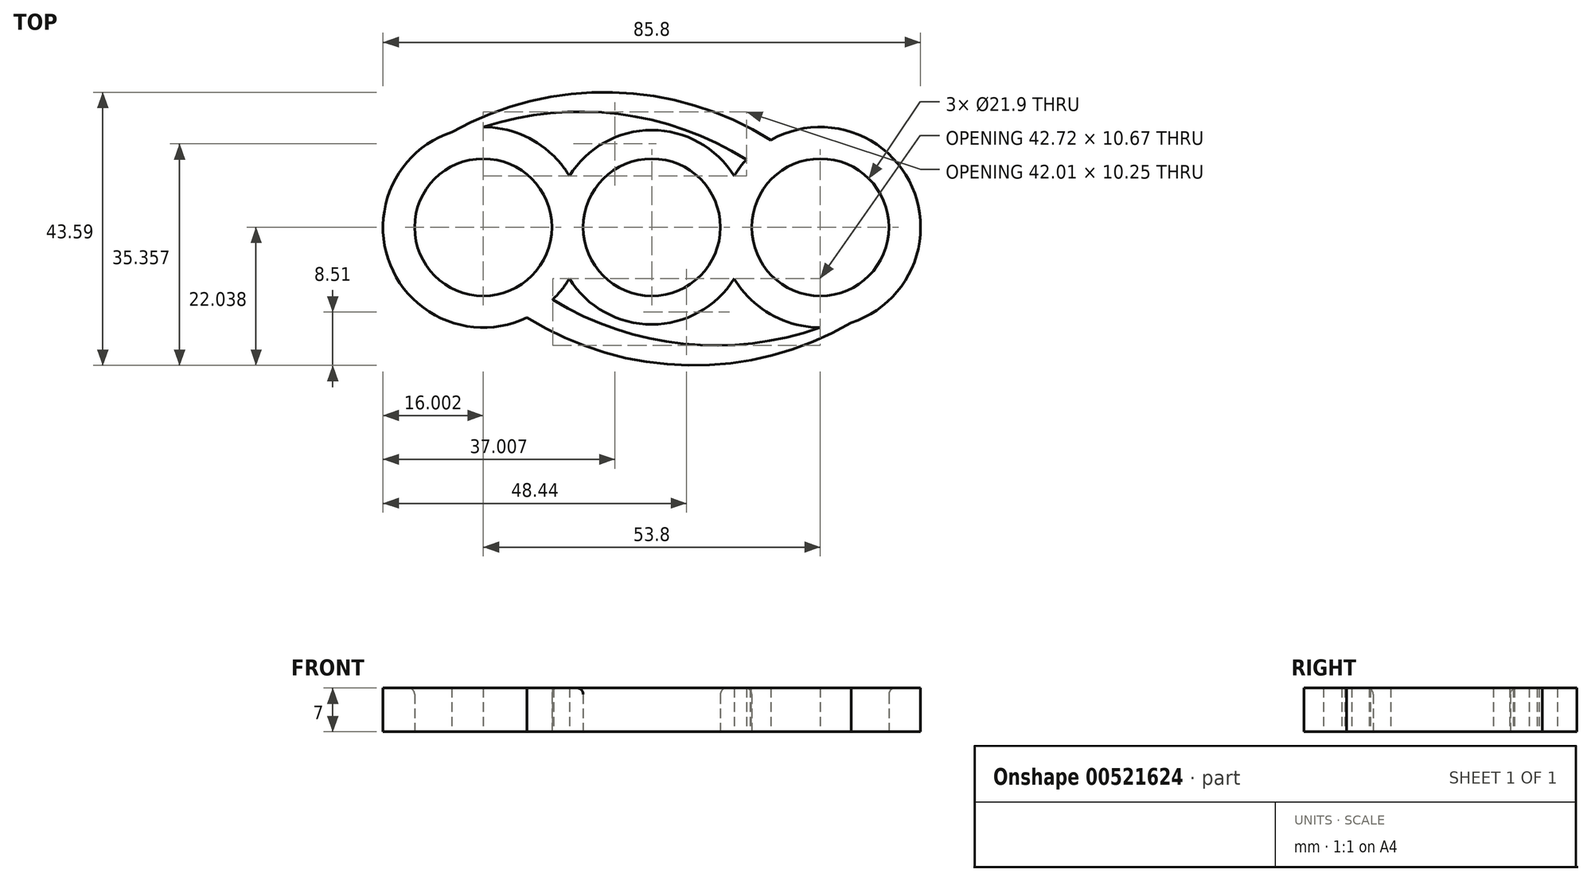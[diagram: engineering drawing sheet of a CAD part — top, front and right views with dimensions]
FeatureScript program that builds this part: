
annotation { "Feature Type Name" : "Feature", "Feature Type Description" : "" }
export const myFeature = defineFeature(function(context is Context, id is Id, definition is map)
    precondition{}
    {
        {
            var Q0;
            Q0=qCreatedBy(makeId("Top.planeOp"),FACE);
            var sketch = newSketch(context, id + "F0", { "sketchPlane" : qUnion([Q0])});
            skCircle(sketch, "E0", {"center": v(-8.38, 3.3) * mm, "radius": 10.95 * mm});
            skCircle(sketch, "E1", {"center": v(-35.28, 3.3) * mm, "radius": 10.95 * mm});
            skCircle(sketch, "E2", {"center": v(18.52, 3.3) * mm, "radius": 10.95 * mm});
            skCircle(sketch, "E3", {"center": v(-35.28, 3.3) * mm, "radius": 16 * mm});
            skCircle(sketch, "E4", {"center": v(-8.38, 3.3) * mm, "radius": 15.5 * mm});
            skCircle(sketch, "E5", {"center": v(18.52, 3.3) * mm, "radius": 16 * mm});
            skArc(sketch, "E6", {"start": v(-19.43, -7.57) * mm, "mid": v(-21.93, -7.1) * mm, "end": v(-24.2, -8.25) * mm});
            skPoint(sketch, "E6.startSnap0", {"position": v(-19.43, -4.4) * mm});
            skArc(sketch, "E7", {"start": v(7.47, -8.27) * mm, "mid": v(5.2, -7.11) * mm, "end": v(2.67, -7.57) * mm});
            skArc(sketch, "E8", {"start": v(2.67, 14.17) * mm, "mid": v(4.7, 13.59) * mm, "end": v(6.73, 14.12) * mm});
            skArc(sketch, "E9", {"start": v(-24.23, 14.87) * mm, "mid": v(-21.95, 13.7) * mm, "end": v(-19.43, 14.17) * mm});
            skArc(sketch, "E10", {"start": v(6.73, 14.12) * mm, "mid": v(-13.7, 21.37) * mm, "end": v(-35.28, 19.3) * mm});
            skArc(sketch, "E11", {"start": v(-24.2, -8.25) * mm, "mid": v(-3.34, -15.3) * mm, "end": v(18.52, -12.7) * mm});
            skArc(sketch, "E12", {"start": v(-28.3, -11.1) * mm, "mid": v(-2.54, -18.73) * mm, "end": v(23.46, -11.92) * mm});
            skArc(sketch, "E13", {"start": v(10.65, 17.23) * mm, "mid": v(-14.64, 24.83) * mm, "end": v(-40.28, 18.5) * mm});
            skSolve(sketch);
        }
        {
            var Q0;
            Q0=makeQuery(id+"F0.imprint","IMPRINT",FACE,{"disambiguationData":[TD([[makeQuery(id+"F0.imprint","IMPRINT",EDGE,{"derivedFrom":sQuery(id+"F0.wireOp",EDGE,"E1")}),-1.0]])]});
            var Q1;
            {var subQ0=sQuery(id+"F0.wireOp",EDGE,"E10");Q1=makeQuery(id+"F0.imprint","IMPRINT",FACE,{"disambiguationData":[TD([[makeQuery(id+"F0.imprint","IMPRINT",EDGE,{"derivedFrom":subQ0}),-1.0]])]});}
            var Q2;
            {var subQ5=sQuery(id+"F0.wireOp",EDGE,"E3");var subQ6=sQuery(id+"F0.wireOp",EDGE,"E0");var subQ7=makeQuery(id+"F0.imprint","INTERSECT",VERTEX,{"disambiguationData":[OD(0.0)],"derivedFrom":[subQ6,subQ5]});Q2=makeQuery(id+"F0.imprint","IMPRINT",FACE,{"disambiguationData":[TD([[makeQuery(id+"F0.imprint","IMPRINT",EDGE,{"disambiguationData":[TD([[subQ7,1.0]])],"derivedFrom":subQ6}),-1.0]])]});}
            var Q3;
            {var subQ0=sQuery(id+"F0.wireOp",EDGE,"E3");var subQ1=sQuery(id+"F0.wireOp",EDGE,"E0");var subQ2=makeQuery(id+"F0.imprint","INTERSECT",VERTEX,{"disambiguationData":[OD(0.0)],"derivedFrom":[subQ1,subQ0]});Q3=makeQuery(id+"F0.imprint","IMPRINT",FACE,{"disambiguationData":[TD([[makeQuery(id+"F0.imprint","IMPRINT",EDGE,{"disambiguationData":[TD([[subQ2,-1.0]])],"derivedFrom":subQ1}),-1.0]])]});}
            var Q4;
            {var subQ2=sQuery(id+"F0.wireOp",EDGE,"E3");var subQ4=sQuery(id+"F0.wireOp",EDGE,"E0");var subQ5=makeQuery(id+"F0.imprint","INTERSECT",VERTEX,{"disambiguationData":[OD(1.0)],"derivedFrom":[subQ4,subQ2]});Q4=makeQuery(id+"F0.imprint","IMPRINT",FACE,{"disambiguationData":[TD([[makeQuery(id+"F0.imprint","IMPRINT",EDGE,{"disambiguationData":[TD([[subQ5,-1.0]])],"derivedFrom":subQ4}),-1.0]])]});}
            var Q5;
            {var subQ0=sQuery(id+"F0.wireOp",EDGE,"E5");var subQ1=sQuery(id+"F0.wireOp",EDGE,"E0");var subQ2=makeQuery(id+"F0.imprint","INTERSECT",VERTEX,{"disambiguationData":[OD(0.0)],"derivedFrom":[subQ1,subQ0]});Q5=makeQuery(id+"F0.imprint","IMPRINT",FACE,{"disambiguationData":[TD([[makeQuery(id+"F0.imprint","IMPRINT",EDGE,{"disambiguationData":[TD([[subQ2,1.0]])],"derivedFrom":subQ1}),-1.0]])]});}
            var Q6;
            Q6=makeQuery(id+"F0.imprint","IMPRINT",FACE,{"disambiguationData":[TD([[makeQuery(id+"F0.imprint","IMPRINT",EDGE,{"derivedFrom":sQuery(id+"F0.wireOp",EDGE,"E2")}),-1.0]])]});
            var Q7;
            {var subQ0=sQuery(id+"F0.wireOp",EDGE,"E11");Q7=makeQuery(id+"F0.imprint","IMPRINT",FACE,{"disambiguationData":[TD([[makeQuery(id+"F0.imprint","IMPRINT",EDGE,{"derivedFrom":subQ0}),-1.0]])]});}
            extrude(context, id + "F1", {"entities" : qUnion([Q0, Q1, Q2, Q3, Q4, Q5, Q6, Q7]), "depth" : 7 * mm, "offsetDistance" : 25 * mm});
        }
        {
            var Q0;
            Q0=makeQuery(id+"F1.opExtrude","CAP_EDGE",EDGE,{"disambiguationData":[OSD([sQuery(id+"F0.wireOp",EDGE,"E2")])],"isStart":false});
            var Q1;
            Q1=makeQuery(id+"F1.opExtrude","CAP_EDGE",EDGE,{"disambiguationData":[OSD([sQuery(id+"F0.wireOp",EDGE,"E0")])],"isStart":false});
            var Q2;
            Q2=makeQuery(id+"F1.opExtrude","CAP_EDGE",EDGE,{"disambiguationData":[OSD([sQuery(id+"F0.wireOp",EDGE,"E1")])],"isStart":false});
            fillet(context, id + "F2", {"entities" : qUnion([Q0, Q1, Q2]), "radius" : 1 * mm, "tangentPropagation" : true, "allowEdgeOverflow" : false});
        }
    });
